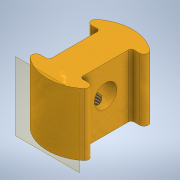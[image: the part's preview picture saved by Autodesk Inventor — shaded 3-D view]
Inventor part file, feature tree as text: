
AUTODESK INVENTOR PART (.ipt)
format: ipt  version: 2020 (Build 240168000, 168)  size: 171,008 bytes
history: native  units: mm
features: sketch x3, hole x2, extrude x1, plane x1, thread x1, fillet x1
ambient origin geometry x8: Origin, YZ Plane, XZ Plane, XY Plane, X Axis, Y Axis, Z Axis, Center Point
bodies: Solid1 (feature_tree)
feature tree (9):
  extrude  "Extrusion1"  Depth=9.0mm
  plane  "Work Plane1"
  hole  "Hole1"  [1 undecoded]
  hole  "Hole2"  [1 undecoded]
  thread  "Thread1"  [1 undecoded]
  fillet  "Fillet1"  Radius=7.5mm
  sketch  "Sketch1"  dims[d0=5.5mm d1=9.0mm]
  sketch  "Sketch2"  dims[d2=9.5mm d3=180.0deg]
  sketch  "Sketch3"  dims[d4=7.5mm d5=9.5mm d6=180.0deg d7=7.5mm d8=15.0mm d10=0.75mm d11=0.75mm d12=0.5mm d13=0.75mm d14=0.75mm d15=0.5mm d16=11.0mm d17=0.0mm d18=7.5mm d19=5.0mm d20=4.0mm d21=6.0mm d22=4.0mm d23=2.0mm d24=90.0deg d25=8.0mm d26=20.594885mm d27=3.0mm d28=6.0mm d29=4.0mm d30=2.0mm d31=90.0deg d32=4.42mm d33=20.594885mm d34=5.5mm d35=0.0mm d36=0.75mm]
note: 3 required parameter values undecoded (feature->parameter linkage not recoverable at this tier; creation-order binding heuristic only, values carry confidence <= 0.55)
